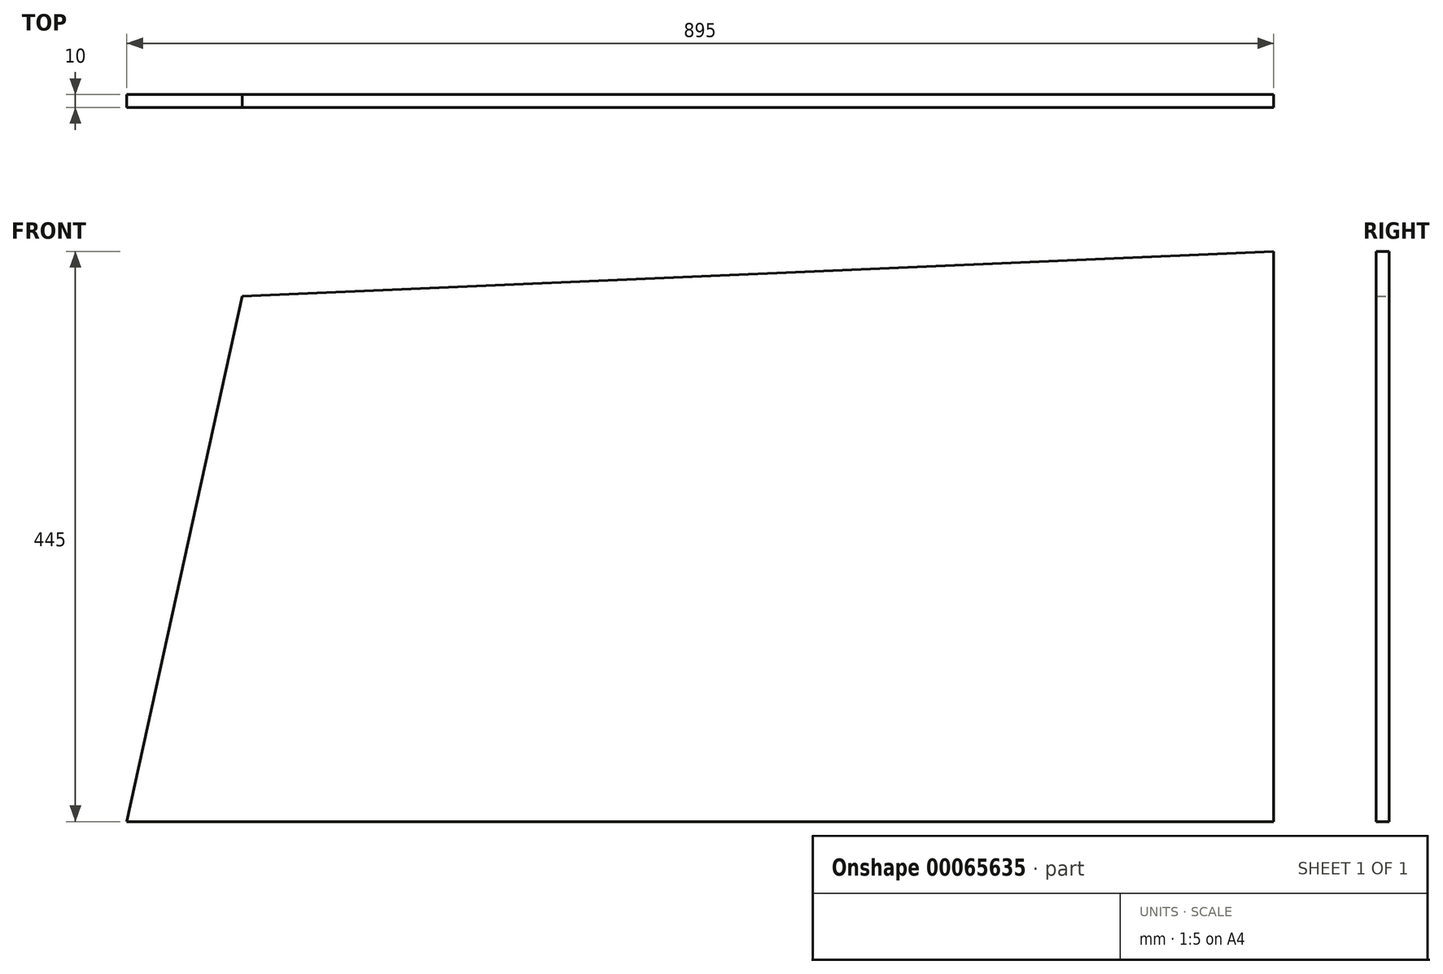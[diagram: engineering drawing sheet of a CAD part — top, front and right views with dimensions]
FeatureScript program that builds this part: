
annotation { "Feature Type Name" : "Feature", "Feature Type Description" : "" }
export const myFeature = defineFeature(function(context is Context, id is Id, definition is map)
    precondition{}
    {
        {
            var Q0;
            Q0=qCreatedBy(makeId("Front.planeOp"),FACE);
            var sketch = newSketch(context, id + "F0", { "sketchPlane" : qUnion([Q0])});
            skLineSegment(sketch, "E0", {"start": v(-895, 0) * mm, "end": v(0, 0) * mm});
            skLineSegment(sketch, "E1", {"start": v(0, 0) * mm, "end": v(0, 445) * mm});
            skLineSegment(sketch, "E2", {"start": v(0, 445) * mm, "end": v(-804.88, 410) * mm});
            skLineSegment(sketch, "E3", {"start": v(-804.88, 410) * mm, "end": v(-895, 0) * mm});
            skLineSegment(sketch, "E4", {"start": v(-804.88, 410) * mm, "end": v(-804.88, 0) * mm, "construction": true});
            skSolve(sketch);
        }
        {
            var Q0;
            Q0 = qSketchRegion(id + "F0", true);
            extrude(context, id + "F1", {"entities" : qUnion([Q0]), "depth" : 10 * mm});
        }
    });
